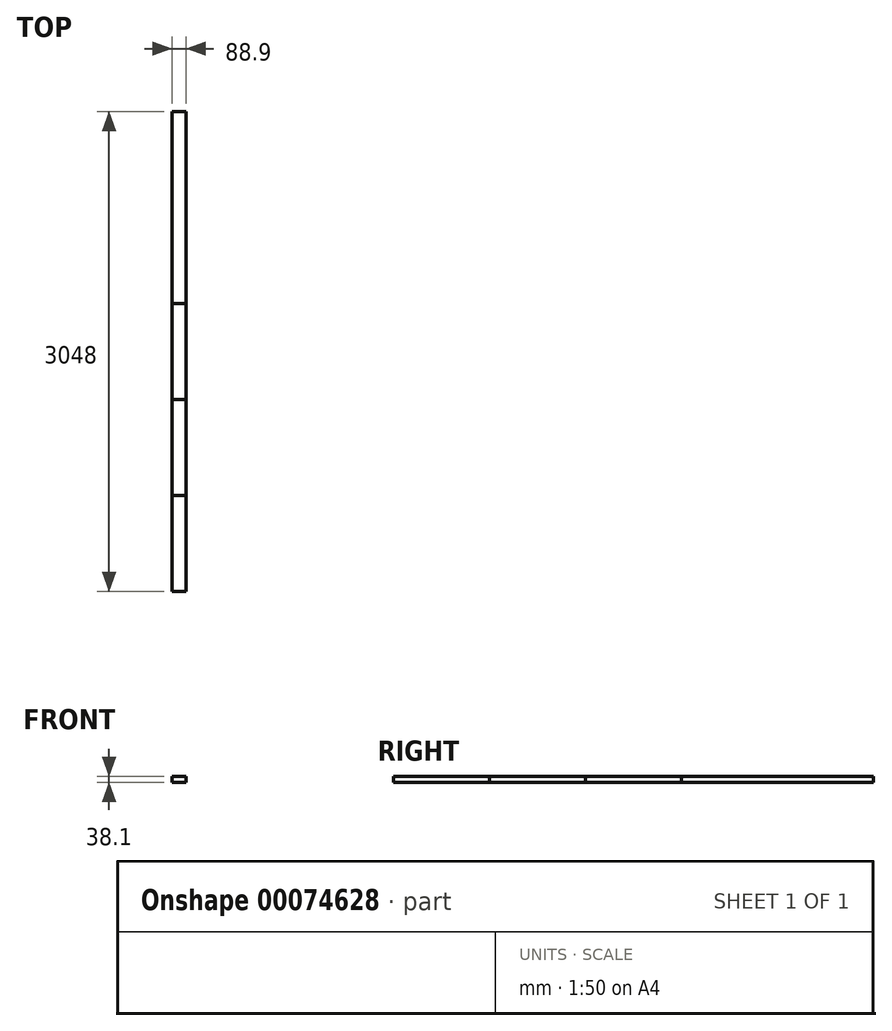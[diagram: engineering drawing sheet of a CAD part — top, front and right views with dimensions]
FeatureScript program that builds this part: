
annotation { "Feature Type Name" : "Feature", "Feature Type Description" : "" }
export const myFeature = defineFeature(function(context is Context, id is Id, definition is map)
    precondition{}
    {
        {
            var Q0;
            Q0=qCreatedBy(makeId("Front.planeOp"),FACE);
            var sketch = newSketch(context, id + "F0", { "sketchPlane" : qUnion([Q0])});
            skLineSegment(sketch, "E0.bottom", {"start": v(44.45, -19.05) * mm, "end": v(-44.45, -19.05) * mm});
            skLineSegment(sketch, "E0.top", {"start": v(44.45, 19.05) * mm, "end": v(-44.45, 19.05) * mm});
            skLineSegment(sketch, "E0.left", {"start": v(44.45, -19.05) * mm, "end": v(44.45, 19.05) * mm});
            skLineSegment(sketch, "E0.right", {"start": v(-44.45, -19.05) * mm, "end": v(-44.45, 19.05) * mm});
            skPoint(sketch, "E0.middle", {"position": v(0, 0) * mm});
            skSolve(sketch);
        }
        {
            var Q0;
            Q0 = qSketchRegion(id + "F0", true);
            extrude(context, id + "F1", {"entities" : qUnion([Q0]), "depth" : 2438.4 * mm});
        }
        {
            var Q0;
            Q0=makeQuery(id+"F0.imprint","IMPRINT",FACE,{"disambiguationData":[TD([[makeQuery(id+"F0.imprint","IMPRINT",EDGE,{"derivedFrom":sQuery(id+"F0.wireOp",EDGE,"E0.bottom")}),-1.0]])]});
            extrude(context, id + "F2", {"entities" : qUnion([Q0]), "depth" : 3048 * mm});
        }
        {
            var Q0;
            Q0 = qSketchRegion(id + "F0", true);
            extrude(context, id + "F3", {"entities" : qUnion([Q0]), "depth" : 1828.8 * mm});
        }
        {
            var Q0;
            Q0 = qSketchRegion(id + "F0", true);
            extrude(context, id + "F4", {"entities" : qUnion([Q0]), "depth" : 1219.2 * mm});
        }
    });
